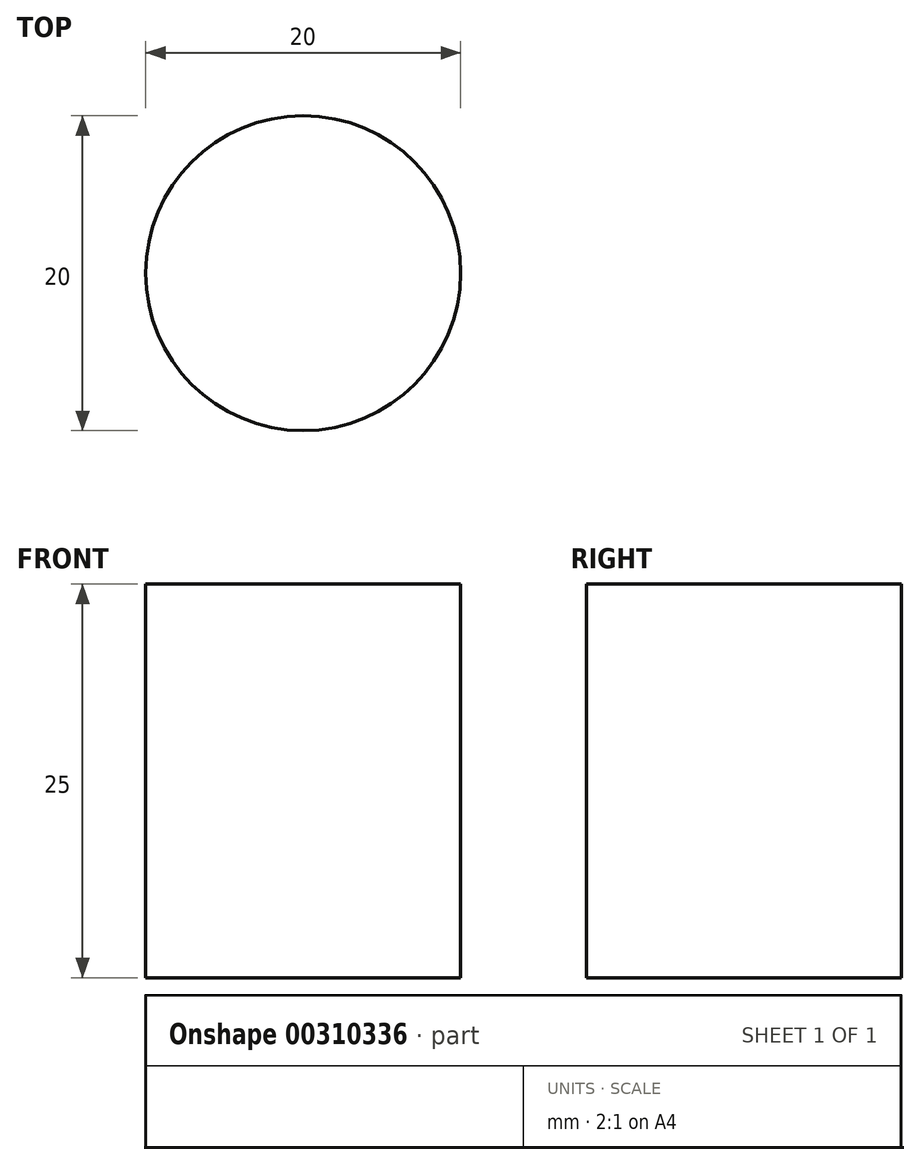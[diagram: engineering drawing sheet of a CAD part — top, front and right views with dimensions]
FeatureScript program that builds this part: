
annotation { "Feature Type Name" : "Feature", "Feature Type Description" : "" }
export const myFeature = defineFeature(function(context is Context, id is Id, definition is map)
    precondition{}
    {
        {
            var Q0;
            Q0=qCreatedBy(makeId("Top.planeOp"),FACE);
            var sketch = newSketch(context, id + "F0", { "sketchPlane" : qUnion([Q0])});
            skCircle(sketch, "E0", {"center": v(0, 0) * mm, "radius": 10 * mm});
            skSolve(sketch);
        }
        {
            var Q0;
            Q0=makeQuery(id+"F0.imprint","IMPRINT",FACE,{"disambiguationData":[TD([[makeQuery(id+"F0.imprint","IMPRINT",EDGE,{"derivedFrom":sQuery(id+"F0.wireOp",EDGE,"E0")}),1.0]])]});
            extrude(context, id + "F1", {"entities" : qUnion([Q0]), "depth" : 25 * mm});
        }
    });
